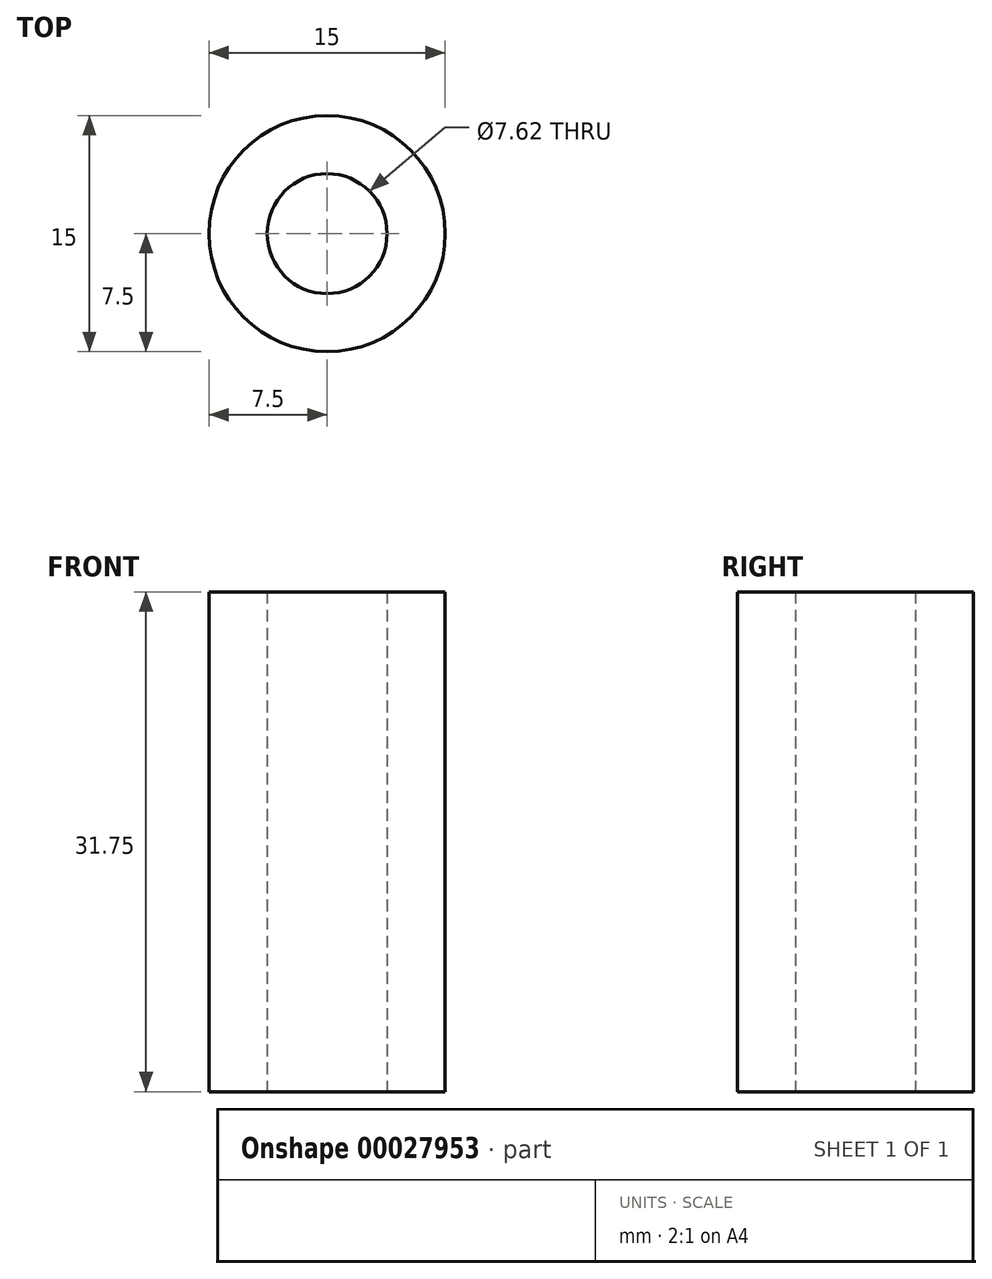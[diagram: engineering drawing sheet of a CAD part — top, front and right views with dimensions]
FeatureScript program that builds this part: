
annotation { "Feature Type Name" : "Feature", "Feature Type Description" : "" }
export const myFeature = defineFeature(function(context is Context, id is Id, definition is map)
    precondition{}
    {
        {
            var Q0;
            Q0=qCreatedBy(makeId("Top.planeOp"),FACE);
            var sketch = newSketch(context, id + "F0", { "sketchPlane" : qUnion([Q0])});
            skCircle(sketch, "E0", {"center": v(0, 0) * mm, "radius": 3.81 * mm});
            skCircle(sketch, "E1", {"center": v(0, 0) * mm, "radius": 7.5 * mm});
            skSolve(sketch);
        }
        {
            var Q0;
            Q0=makeQuery(id+"F0.imprint","IMPRINT",FACE,{"disambiguationData":[TD([[makeQuery(id+"F0.imprint","IMPRINT",EDGE,{"derivedFrom":sQuery(id+"F0.wireOp",EDGE,"E0")}),-1.0]])]});
            extrude(context, id + "F1", {"entities" : qUnion([Q0]), "depth" : 31.75 * mm});
        }
    });
